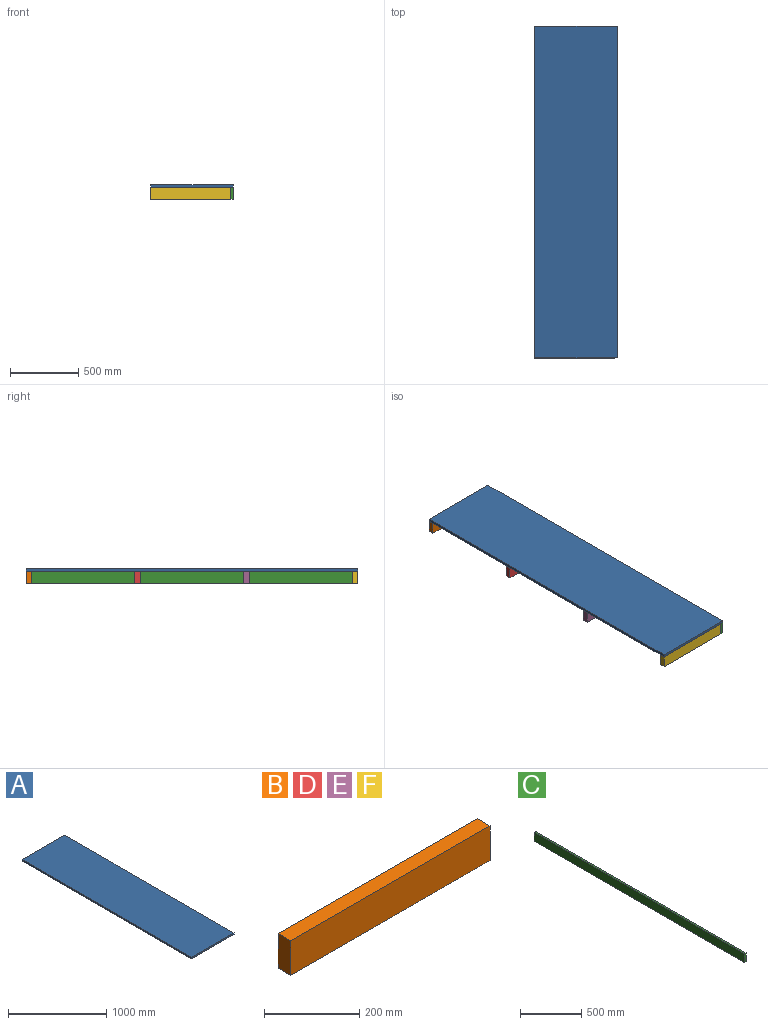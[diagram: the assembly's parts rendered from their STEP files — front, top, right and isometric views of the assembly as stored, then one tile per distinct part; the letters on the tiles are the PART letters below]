
ASSEMBLY  parts=6 mates=5
PART A: 6 faces, bbox 609.6x2438.4x19.1 mm
  f0: plane 2438.4x19.05mm, normal (-1,0,0), area 46451.5mm2, adj f1,f3,f4,f5
  f1: plane 609.6x19.05mm, normal (0,-1,0), area 11612.9mm2, adj f0,f2,f4,f5
  f2: plane 2438.4x19.05mm, normal (1,0,0), area 46451.5mm2, adj f1,f3,f4,f5
  f3: plane 609.6x19.05mm, normal (0,1,0), area 11612.9mm2, adj f0,f2,f4,f5
  f4: plane 2438.4x609.6mm, normal (0,0,1), area 1486448.6mm2, adj f0,f1,f2,f3
  f5: plane 2438.4x609.6mm, normal (0,0,-1), area 1486448.6mm2, adj f0,f1,f2,f3
PART B: 6 faces, bbox 590.6x38.1x88.9 mm
  f0: plane 590.55x88.9mm, normal (0,1,0), area 52499.9mm2, adj f1,f3,f4,f5
  f1: plane 88.9x38.1mm, normal (-1,0,0), area 3387.1mm2, adj f0,f2,f4,f5
  f2: plane 590.55x88.9mm, normal (0,-1,0), area 52499.9mm2, adj f1,f3,f4,f5
  f3: plane 88.9x38.1mm, normal (1,0,0), area 3387.1mm2, adj f0,f2,f4,f5
  f4: plane 590.55x38.1mm, normal (0,0,1), area 22500mm2, adj f0,f1,f2,f3
  f5: plane 590.55x38.1mm, normal (0,0,-1), area 22500mm2, adj f0,f1,f2,f3
PART C: 6 faces, bbox 19.1x2438.4x88.9 mm
  f0: plane 2438.4x19.05mm, normal (0,0,1), area 46451.5mm2, adj f1,f3,f4,f5
  f1: plane 88.9x19.05mm, normal (0,-1,0), area 1693.5mm2, adj f0,f2,f3,f4
  f2: plane 2438.4x19.05mm, normal (0,0,-1), area 46451.5mm2, adj f1,f3,f4,f5
  f3: plane 2438.4x88.9mm, normal (1,0,0), area 216773.8mm2, adj f0,f1,f2,f5
  f4: plane 2438.4x88.9mm, normal (-1,0,0), area 216773.8mm2, adj f0,f1,f2,f5
  f5: plane 88.9x19.05mm, normal (0,1,0), area 1693.5mm2, adj f0,f2,f3,f4
PART D: same geometry as B
PART E: same geometry as B
PART F: same geometry as B
PLACE A t=(-333.12,39.51,148.56)mm
PLACE B t=(-333.12,2477.91,59.66)mm
PLACE C t=(-27.42,-227.34,-14.96)mm
PLACE D t=(-333.12,1677.81,59.66)mm
PLACE E t=(-333.12,877.71,59.66)mm
PLACE F t=(-333.12,77.61,59.66)mm
MATE fastened E.f3 <-> F.f3  axis (1,0,0) through (257.43,839.61,148.56)mm
MATE fastened C.f1 <-> F.f2  axis (0,-1,0) through (257.43,39.51,148.56)mm
MATE fastened D.f3 <-> B.f3  axis (1,0,0) through (257.43,1677.81,148.56)mm
MATE fastened F.f1 <-> A.f0  axis (-1,0,0) through (-333.12,39.51,148.56)mm
MATE fastened B.f1 <-> A.f0  axis (-1,0,0) through (-333.12,2477.91,148.56)mm
